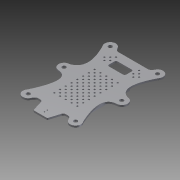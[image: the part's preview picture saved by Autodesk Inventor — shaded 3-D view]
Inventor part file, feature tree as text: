
AUTODESK INVENTOR PART (.ipt)
format: ipt  version: 2015 (Build 190159000, 159)  size: 697,344 bytes
history: native  units: mm
features: sketch x3, extrude x2, hole x2
ambient origin geometry x8: Origin, YZ Plane, XZ Plane, XY Plane, X Axis, Y Axis, Z Axis, Center Point
bodies: Solid1 (feature_tree)
feature tree (7):
  sketch  "Sketch1"  dims[d0=10.0mm d1=6.5mm d2=6.5mm d3=6.5mm d4=6.5mm d5=6.5mm d6=12.0mm d7=2.0mm d8=2.0mm d9=5.0mm d10=5.0mm d11=71.014083mm d12=41.0mm d13=3.0mm d14=3.0mm d15=3.0mm d16=3.0mm d17=3.0mm d18=3.0mm d19=3.0mm d20=3.0mm d21=10.0mm d22=3.0mm d23=3.0mm d24=3.0mm d25=10.0mm d26=12.5mm d27=12.5mm d28=12.5mm d29=12.5mm d30=8.00764mm d31=17.45764mm d32=8.00764mm d33=12.118872mm d34=2.0mm d35=10.0mm d36=10.0mm d37=10.0mm d38=10.0mm d39=10.0mm d40=10.0mm d41=10.0mm d42=10.0mm d43=3.0mm d44=3.0mm d45=3.0mm d46=3.0mm d47=18.0mm d48=5.0mm d49=1.0mm d50=18.0mm d51=18.0mm d52=10.0mm d53=10.0mm d54=10.0mm d55=6.5mm d56=3.0mm d57=3.0mm d58=3.0mm d59=3.0mm d60=3.0mm d61=3.0mm d62=3.0mm d63=10.0mm d64=3.0mm d65=3.0mm d66=3.0mm d67=10.0mm d68=3.0mm d69=3.0mm d70=3.0mm d71=10.0mm d72=3.0mm d73=3.0mm d74=3.0mm d75=10.0mm d76=3.0mm d77=3.0mm d78=3.0mm d79=10.0mm d80=3.0mm d81=3.0mm d82=3.0mm d83=10.0mm d84=3.0mm d85=3.0mm d86=3.0mm d87=10.0mm d88=3.0mm d89=3.0mm d90=3.0mm d91=10.0mm d92=3.0mm d93=3.0mm d94=3.0mm d95=10.0mm d96=3.0mm d97=0.0mm]
  extrude  "Extrusion1"  Depth=10.0mm TaperAngle=0.0deg
  hole  "Hole1"  [1 undecoded]
  hole  "Hole2"  [1 undecoded]
  extrude  "Extrusion2"  [1 undecoded]
  sketch  "Sketch2"  dims[d98=10.0mm d99=6.5mm d100=6.5mm d101=6.5mm d102=6.5mm d103=6.5mm d104=12.0mm d105=2.0mm d106=2.0mm d107=5.0mm d108=5.0mm d109=71.014083mm d110=41.0mm d111=3.0mm d112=3.0mm d113=3.0mm d114=3.0mm d115=3.0mm d116=3.0mm d117=3.0mm d118=3.0mm d119=10.0mm d120=3.0mm d121=3.0mm d122=3.0mm d123=10.0mm d124=12.5mm d125=12.5mm d126=12.5mm d127=12.5mm d128=8.00764mm d129=17.45764mm d130=8.00764mm d131=12.118872mm d132=2.0mm d133=10.0mm d134=10.0mm d135=10.0mm d136=10.0mm d137=10.0mm d138=10.0mm d139=10.0mm d140=10.0mm d141=3.0mm d142=3.0mm d143=3.0mm d144=3.0mm d145=18.0mm d146=5.0mm d147=1.0mm d148=18.0mm d149=18.0mm d150=10.0mm d151=10.0mm d152=10.0mm d153=6.5mm d154=3.0mm d155=3.0mm d156=3.0mm d157=3.0mm d158=3.0mm d159=3.0mm d160=3.0mm d161=10.0mm d162=3.0mm d163=3.0mm d164=3.0mm d165=10.0mm d166=3.0mm d167=3.0mm d168=3.0mm d169=10.0mm d170=3.0mm d171=3.0mm d172=3.0mm d173=10.0mm d174=3.0mm d175=3.0mm d176=3.0mm d177=10.0mm d178=3.0mm d179=3.0mm d180=3.0mm d181=10.0mm d182=3.0mm d183=3.0mm d184=3.0mm d185=10.0mm d186=3.0mm d187=3.0mm d188=3.0mm d189=10.0mm d190=3.0mm d191=3.0mm d192=3.0mm d193=10.0mm d194=6.5mm d195=6.0mm d196=4.0mm d197=2.0mm d198=90.0deg d199=8.0mm d200=20.594885mm]
  sketch  "Sketch3"  dims[d201=10.0mm d202=6.5mm d203=6.5mm d204=6.5mm d205=6.5mm d206=6.5mm d207=12.0mm d208=2.0mm d209=2.0mm d210=5.0mm d211=5.0mm d212=71.014083mm d213=41.0mm d214=3.0mm d215=3.0mm d216=3.0mm d217=3.0mm d218=3.0mm d219=3.0mm d220=3.0mm d221=3.0mm d222=10.0mm d223=3.0mm d224=3.0mm d225=3.0mm d226=10.0mm d227=12.5mm d228=12.5mm d229=12.5mm d230=12.5mm d231=8.00764mm d232=17.45764mm d233=8.00764mm d234=12.118872mm d235=2.0mm d236=10.0mm d237=10.0mm d238=10.0mm d239=10.0mm d240=10.0mm d241=10.0mm d242=10.0mm d243=10.0mm d244=3.0mm d245=3.0mm d246=3.0mm d247=3.0mm d248=18.0mm d249=5.0mm d250=1.0mm d251=18.0mm d252=18.0mm d253=10.0mm d254=10.0mm d255=10.0mm d256=6.5mm d257=3.0mm d258=3.0mm d259=3.0mm d260=3.0mm d261=3.0mm d262=3.0mm d263=3.0mm d264=10.0mm d265=3.0mm d266=3.0mm d267=3.0mm d268=10.0mm d269=3.0mm d270=3.0mm d271=3.0mm d272=10.0mm d273=3.0mm d274=3.0mm d275=3.0mm d276=10.0mm d277=3.0mm d278=3.0mm d279=3.0mm d280=10.0mm d281=3.0mm d282=3.0mm d283=3.0mm d284=10.0mm d285=3.0mm d286=3.0mm d287=3.0mm d288=10.0mm d289=3.0mm d290=3.0mm d291=3.0mm d292=10.0mm d293=3.0mm d294=3.0mm d295=3.0mm d296=10.0mm d297=3.0mm d298=6.0mm d299=4.0mm d300=2.0mm d301=90.0deg d302=8.0mm d303=20.594885mm d304=10.0mm d305=0.0mm d306=19.985917mm]
note: 3 required parameter values undecoded (feature->parameter linkage not recoverable at this tier; creation-order binding heuristic only, values carry confidence <= 0.55)
